# Revit family: Table-Teknion-CFTBFG_Figure_Table_Rectangular_Gable_Leg_Bullnose_Flat_Edge-R2023
name_source: partatom
category: Furniture
units: mm (PartAtom-declared; Revit-internal decimal feet)

## family parameters
Always vertical = Yes
Cut with Voids When Loaded = No
Enable Cutting in Views = No
OmniClass Number = 23.40.20.00
OmniClass Title = General Furniture and Specialties
Render Appearance Source = Family Geometry
Room Calculation Point = No
Shared = Yes
Work Plane-Based = No

## types (3) — shared parameters
Assembly Code = E2020200
Manufacturer = Teknion
Manufacturer Fax = 416.661.4586
Part Number = CFTBFG
Product Line = Figure Table
Product Page URL = https://www.teknion.com
Series = Custom Wood Boardroom & Reception Tables
Sustainability Data = https://www.teknion.com
URL = www.teknion.com
Unit Weight URL = http://www.teknion.com
Warranty = http://www.teknion.com
zero-valued in all types: Default Elevation

## per-type parameters (varying)
| type | Description | H - Hexa Panel | Model | N - No Central Base | S - Softened Panel |
| No Central Base | Figure Table, Rectangular, Gable Leg, Bullnose Flat Edge, No Central Base, Square Corner | No | CFTBFG__NS_ | Yes | No |
| Softened Panel Central Base | Figure Table, Rectangular, Gable Leg, Bullnose Flat Edge, Softened Panel Central Base, Square Corner | No | CFTBFG__SS_ | No | Yes |
| Hexa Panel Central Base | Figure Table, Rectangular, Gable Leg, Bullnose Flat Edge, Hexa Panel Central Base, Square Corner | Yes | CFTBFG__HS_ | No | No |

## geometry (parser evidence)
native form markers: Sweep x13
no freeform markers — native parametric forms only
